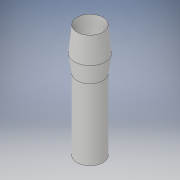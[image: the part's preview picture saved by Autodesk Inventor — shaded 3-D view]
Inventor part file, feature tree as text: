
AUTODESK INVENTOR PART (.ipt)
format: ipt  version: 2017 (Build 210142000, 142)  size: 111,616 bytes
history: native  units: in
note: dims shown in document units (in); Inventor stores cm internally (conversion verified against a paired STEP export)
features: revolve x1, sketch x1
ambient origin geometry x8: Origin, YZ Plane, XZ Plane, XY Plane, X Axis, Y Axis, Z Axis, Center Point
bodies: Solid1 (feature_tree)
feature tree (2):
  revolve  "Revolution1"  [1 undecoded]
  sketch  "Sketch1"  dims[d0=0.475in d1=3.6in d2=0.05in d3=1.0in d4=0.1in d5=90.0deg]
note: 1 required parameter value undecoded (feature->parameter linkage not recoverable at this tier; creation-order binding heuristic only, values carry confidence <= 0.55)
